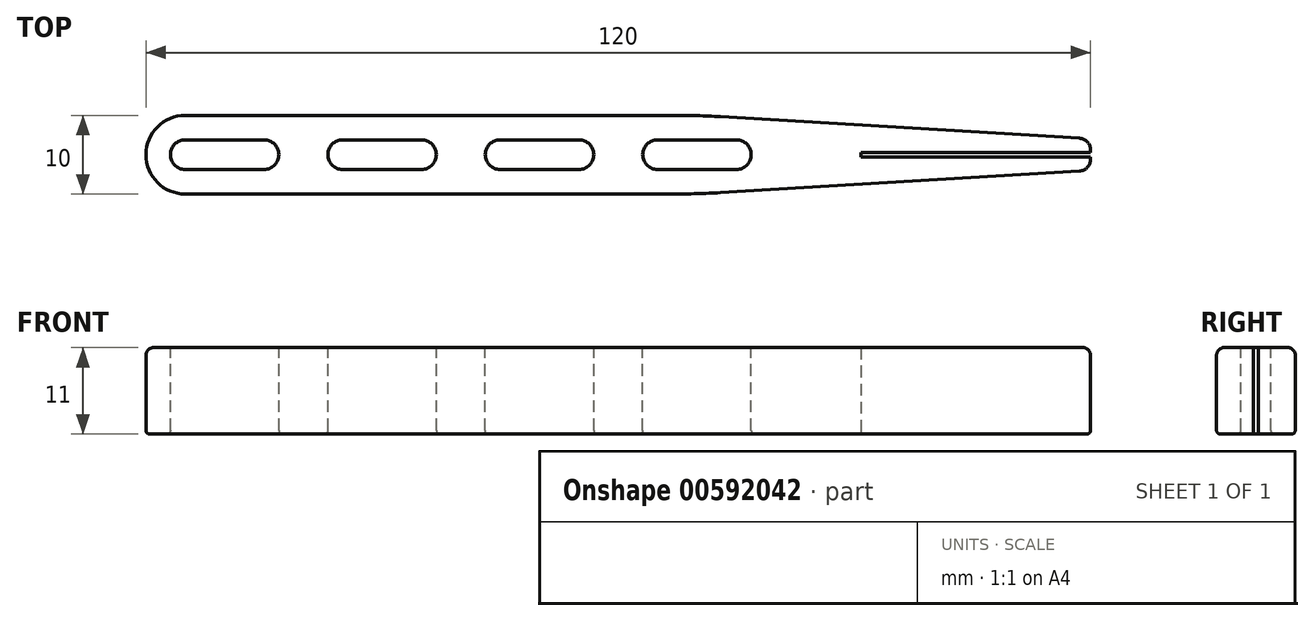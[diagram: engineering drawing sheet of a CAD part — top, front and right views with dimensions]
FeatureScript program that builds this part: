
annotation { "Feature Type Name" : "Feature", "Feature Type Description" : "" }
export const myFeature = defineFeature(function(context is Context, id is Id, definition is map)
    precondition{}
    {
        {
            var Q0;
            Q0=qCreatedBy(makeId("Top.planeOp"),FACE);
            var sketch = newSketch(context, id + "F0", { "sketchPlane" : qUnion([Q0])});
            skLineSegment(sketch, "E0.bottom", {"start": v(-60.45, 1.98) * mm, "end": v(59.55, 1.98) * mm});
            skLineSegment(sketch, "E0.top", {"start": v(-60.45, -8.02) * mm, "end": v(59.55, -8.02) * mm});
            skLineSegment(sketch, "E0.left", {"start": v(-60.45, 1.98) * mm, "end": v(-60.45, -8.02) * mm});
            skLineSegment(sketch, "E1", {"start": v(59.55, -2.72) * mm, "end": v(30.4, -2.72) * mm});
            skLineSegment(sketch, "E2", {"start": v(30.4, -2.72) * mm, "end": v(30.4, -3.32) * mm});
            skLineSegment(sketch, "E3", {"start": v(30.4, -3.32) * mm, "end": v(59.55, -3.32) * mm});
            skLineSegment(sketch, "E4", {"start": v(59.55, 1.98) * mm, "end": v(59.55, -2.72) * mm});
            skLineSegment(sketch, "E5", {"start": v(59.55, -8.02) * mm, "end": v(59.55, -3.32) * mm});
            skSolve(sketch);
        }
        {
            var Q0;
            Q0=makeQuery(id+"F0.imprint","IMPRINT",FACE,{"disambiguationData":[TD([[makeQuery(id+"F0.imprint","IMPRINT",EDGE,{"derivedFrom":sQuery(id+"F0.wireOp",EDGE,"E0.bottom")}),-1.0]])]});
            extrude(context, id + "F1", {"entities" : qUnion([Q0]), "depth" : 11 * mm, "offsetDistance" : 25 * mm});
        }
        {
            var Q0;
            Q0=makeQuery(id+"F1.opExtrude","SWEPT_EDGE",EDGE,{"disambiguationData":[OSD([sQuery(id+"F0.wireOp",EDGE,"E0.top"),sQuery(id+"F0.wireOp",EDGE,"E5")])]});
            chamfer(context, id + "F2", {"entities" : qUnion([Q0]), "chamferType" : ChamferType.TWO_OFFSETS, "width1" : 3 * mm, "oppositeDirection" : false, "width2" : 50 * mm, "tangentPropagation" : true});
        }
        {
            var Q0;
            Q0=makeQuery(id+"F1.opExtrude","SWEPT_EDGE",EDGE,{"disambiguationData":[OSD([sQuery(id+"F0.wireOp",EDGE,"E0.bottom"),sQuery(id+"F0.wireOp",EDGE,"E4")])]});
            chamfer(context, id + "F3", {"entities" : qUnion([Q0]), "chamferType" : ChamferType.TWO_OFFSETS, "width1" : 3 * mm, "oppositeDirection" : true, "width2" : 50 * mm, "tangentPropagation" : true});
        }
        {
            var Q0;
            {var subQ0=sQuery(id+"F0.wireOp",EDGE,"E4");Q0=makeQuery(id+"F3.opChamfer","BLEND_EDGE",EDGE,{"blendedFrom":[makeQuery(id+"F1.opExtrude","SWEPT_EDGE",EDGE,{"disambiguationData":[OSD([sQuery(id+"F0.wireOp",EDGE,"E0.bottom"),subQ0])]}),makeQuery(id+"F1.opExtrude","SWEPT_FACE",FACE,{"disambiguationData":[OSD([subQ0])]})],"blendedInto":[makeQuery(id+"F1.opExtrude","SWEPT_FACE",FACE,{"disambiguationData":[OSD([subQ0])]})]});}
            var Q1;
            {var subQ0=sQuery(id+"F0.wireOp",EDGE,"E5");Q1=makeQuery(id+"F2.opChamfer","BLEND_EDGE",EDGE,{"blendedFrom":[makeQuery(id+"F1.opExtrude","SWEPT_EDGE",EDGE,{"disambiguationData":[OSD([sQuery(id+"F0.wireOp",EDGE,"E0.top"),subQ0])]}),makeQuery(id+"F1.opExtrude","SWEPT_FACE",FACE,{"disambiguationData":[OSD([subQ0])]})],"blendedInto":[makeQuery(id+"F1.opExtrude","SWEPT_FACE",FACE,{"disambiguationData":[OSD([subQ0])]})]});}
            fillet(context, id + "F4", {"entities" : qUnion([Q0, Q1]), "radius" : 1.5 * mm, "tangentPropagation" : true, "allowEdgeOverflow" : false});
        }
        {
            var Q0;
            {var subQ0=sQuery(id+"F0.wireOp",EDGE,"E0.top");Q0=makeQuery(id+"F2.opChamfer","BLEND_EDGE",EDGE,{"blendedFrom":[makeQuery(id+"F1.opExtrude","SWEPT_EDGE",EDGE,{"disambiguationData":[OSD([subQ0,sQuery(id+"F0.wireOp",EDGE,"E5")])]}),makeQuery(id+"F1.opExtrude","SWEPT_FACE",FACE,{"disambiguationData":[OSD([subQ0])]})],"blendedInto":[makeQuery(id+"F1.opExtrude","SWEPT_FACE",FACE,{"disambiguationData":[OSD([subQ0])]})]});}
            var Q1;
            {var subQ0=sQuery(id+"F0.wireOp",EDGE,"E0.bottom");Q1=makeQuery(id+"F3.opChamfer","BLEND_EDGE",EDGE,{"blendedFrom":[makeQuery(id+"F1.opExtrude","SWEPT_EDGE",EDGE,{"disambiguationData":[OSD([subQ0,sQuery(id+"F0.wireOp",EDGE,"E4")])]}),makeQuery(id+"F1.opExtrude","SWEPT_FACE",FACE,{"disambiguationData":[OSD([subQ0])]})],"blendedInto":[makeQuery(id+"F1.opExtrude","SWEPT_FACE",FACE,{"disambiguationData":[OSD([subQ0])]})]});}
            fillet(context, id + "F5", {"entities" : qUnion([Q0, Q1]), "radius" : 100 * mm, "tangentPropagation" : true, "allowEdgeOverflow" : false});
        }
        {
            var Q0;
            Q0=makeQuery(id+"F1.opExtrude","CAP_FACE",FACE,{"disambiguationData":[OSD([sQuery(id+"F0.wireOp",EDGE,"E0.bottom"),sQuery(id+"F0.wireOp",EDGE,"E0.top"),sQuery(id+"F0.wireOp",EDGE,"E0.left"),sQuery(id+"F0.wireOp",EDGE,"E1"),sQuery(id+"F0.wireOp",EDGE,"E2"),sQuery(id+"F0.wireOp",EDGE,"E3"),sQuery(id+"F0.wireOp",EDGE,"E4"),sQuery(id+"F0.wireOp",EDGE,"E5")])],"isStart":false});
            var sketch = newSketch(context, id + "F6", { "sketchPlane" : qUnion([Q0])});
            skLineSegment(sketch, "E6", {"start": v(-59.45, -3.02) * mm, "end": v(30.4, -3.02) * mm, "construction": true});
            skCircle(sketch, "E7", {"center": v(-55.45, -3.02) * mm, "radius": 1.89 * mm});
            skCircle(sketch, "E8.1.0.0", {"center": v(-45.45, -3.02) * mm, "radius": 1.89 * mm});
            skCircle(sketch, "E8.2.0.0", {"center": v(-35.45, -3.02) * mm, "radius": 1.89 * mm});
            skCircle(sketch, "E8.3.0.0", {"center": v(-25.45, -3.02) * mm, "radius": 1.89 * mm});
            skCircle(sketch, "E8.4.0.0", {"center": v(-15.45, -3.02) * mm, "radius": 1.89 * mm});
            skCircle(sketch, "E8.5.0.0", {"center": v(-5.45, -3.02) * mm, "radius": 1.89 * mm});
            skCircle(sketch, "E8.6.0.0", {"center": v(4.55, -3.02) * mm, "radius": 1.89 * mm});
            skCircle(sketch, "E8.7.0.0", {"center": v(14.55, -3.02) * mm, "radius": 1.89 * mm});
            skLineSegment(sketch, "E8.direction1", {"start": v(-55.45, -3.02) * mm, "end": v(-45.45, -3.02) * mm, "construction": true});
            skLineSegment(sketch, "E9", {"start": v(-55.45, -1.13) * mm, "end": v(-45.45, -1.13) * mm});
            skLineSegment(sketch, "E10", {"start": v(-55.45, -4.9) * mm, "end": v(-45.45, -4.9) * mm});
            skLineSegment(sketch, "E11", {"start": v(-35.45, -1.13) * mm, "end": v(-25.45, -1.13) * mm});
            skLineSegment(sketch, "E12", {"start": v(-25.45, -4.9) * mm, "end": v(-35.45, -4.9) * mm});
            skLineSegment(sketch, "E13", {"start": v(-15.45, -4.9) * mm, "end": v(-5.45, -4.9) * mm});
            skLineSegment(sketch, "E14", {"start": v(-5.45, -1.13) * mm, "end": v(-15.45, -1.13) * mm});
            skLineSegment(sketch, "E15", {"start": v(4.55, -1.13) * mm, "end": v(14.55, -1.13) * mm});
            skLineSegment(sketch, "E16", {"start": v(14.55, -4.9) * mm, "end": v(4.55, -4.9) * mm});
            skSolve(sketch);
        }
        {
            var Q0;
            {var subQ0=sQuery(id+"F6.wireOp",EDGE,"E7");var subQ1=makeQuery(id+"F6.imprint","INTERSECT",VERTEX,{"derivedFrom":[subQ0,sQuery(id+"F6.wireOp",EDGE,"E9")]});Q0=makeQuery(id+"F6.imprint","IMPRINT",FACE,{"disambiguationData":[TD([[makeQuery(id+"F6.imprint","IMPRINT",EDGE,{"disambiguationData":[TD([[subQ1,-1.0]])],"derivedFrom":subQ0}),1.0]])]});}
            var Q1;
            {var subQ0=sQuery(id+"F6.wireOp",EDGE,"E9");Q1=makeQuery(id+"F6.imprint","IMPRINT",FACE,{"disambiguationData":[TD([[makeQuery(id+"F6.imprint","IMPRINT",EDGE,{"derivedFrom":subQ0}),-1.0]])]});}
            var Q2;
            {var subQ0=sQuery(id+"F6.wireOp",EDGE,"E8.1.0.0");var subQ1=makeQuery(id+"F6.imprint","INTERSECT",VERTEX,{"derivedFrom":[subQ0,sQuery(id+"F6.wireOp",EDGE,"E9")]});Q2=makeQuery(id+"F6.imprint","IMPRINT",FACE,{"disambiguationData":[TD([[makeQuery(id+"F6.imprint","IMPRINT",EDGE,{"disambiguationData":[TD([[subQ1,-1.0]])],"derivedFrom":subQ0}),1.0]])]});}
            var Q3;
            {var subQ0=sQuery(id+"F6.wireOp",EDGE,"E8.2.0.0");var subQ1=makeQuery(id+"F6.imprint","INTERSECT",VERTEX,{"derivedFrom":[subQ0,sQuery(id+"F6.wireOp",EDGE,"E11")]});Q3=makeQuery(id+"F6.imprint","IMPRINT",FACE,{"disambiguationData":[TD([[makeQuery(id+"F6.imprint","IMPRINT",EDGE,{"disambiguationData":[TD([[subQ1,-1.0]])],"derivedFrom":subQ0}),1.0]])]});}
            var Q4;
            {var subQ0=sQuery(id+"F6.wireOp",EDGE,"E11");Q4=makeQuery(id+"F6.imprint","IMPRINT",FACE,{"disambiguationData":[TD([[makeQuery(id+"F6.imprint","IMPRINT",EDGE,{"derivedFrom":subQ0}),-1.0]])]});}
            var Q5;
            {var subQ0=sQuery(id+"F6.wireOp",EDGE,"E8.3.0.0");var subQ1=makeQuery(id+"F6.imprint","INTERSECT",VERTEX,{"derivedFrom":[subQ0,sQuery(id+"F6.wireOp",EDGE,"E11")]});Q5=makeQuery(id+"F6.imprint","IMPRINT",FACE,{"disambiguationData":[TD([[makeQuery(id+"F6.imprint","IMPRINT",EDGE,{"disambiguationData":[TD([[subQ1,-1.0]])],"derivedFrom":subQ0}),1.0]])]});}
            var Q6;
            {var subQ0=sQuery(id+"F6.wireOp",EDGE,"E8.4.0.0");var subQ1=makeQuery(id+"F6.imprint","INTERSECT",VERTEX,{"derivedFrom":[subQ0,sQuery(id+"F6.wireOp",EDGE,"E13")]});Q6=makeQuery(id+"F6.imprint","IMPRINT",FACE,{"disambiguationData":[TD([[makeQuery(id+"F6.imprint","IMPRINT",EDGE,{"disambiguationData":[TD([[subQ1,1.0]])],"derivedFrom":subQ0}),1.0]])]});}
            var Q7;
            {var subQ0=sQuery(id+"F6.wireOp",EDGE,"E13");Q7=makeQuery(id+"F6.imprint","IMPRINT",FACE,{"disambiguationData":[TD([[makeQuery(id+"F6.imprint","IMPRINT",EDGE,{"derivedFrom":subQ0}),1.0]])]});}
            var Q8;
            {var subQ0=sQuery(id+"F6.wireOp",EDGE,"E8.5.0.0");var subQ1=makeQuery(id+"F6.imprint","INTERSECT",VERTEX,{"derivedFrom":[subQ0,sQuery(id+"F6.wireOp",EDGE,"E13")]});Q8=makeQuery(id+"F6.imprint","IMPRINT",FACE,{"disambiguationData":[TD([[makeQuery(id+"F6.imprint","IMPRINT",EDGE,{"disambiguationData":[TD([[subQ1,1.0]])],"derivedFrom":subQ0}),1.0]])]});}
            var Q9;
            {var subQ0=sQuery(id+"F6.wireOp",EDGE,"E8.6.0.0");var subQ1=makeQuery(id+"F6.imprint","INTERSECT",VERTEX,{"derivedFrom":[subQ0,sQuery(id+"F6.wireOp",EDGE,"E15")]});Q9=makeQuery(id+"F6.imprint","IMPRINT",FACE,{"disambiguationData":[TD([[makeQuery(id+"F6.imprint","IMPRINT",EDGE,{"disambiguationData":[TD([[subQ1,-1.0]])],"derivedFrom":subQ0}),1.0]])]});}
            var Q10;
            {var subQ0=sQuery(id+"F6.wireOp",EDGE,"E15");Q10=makeQuery(id+"F6.imprint","IMPRINT",FACE,{"disambiguationData":[TD([[makeQuery(id+"F6.imprint","IMPRINT",EDGE,{"derivedFrom":subQ0}),-1.0]])]});}
            var Q11;
            {var subQ0=sQuery(id+"F6.wireOp",EDGE,"E8.7.0.0");var subQ1=makeQuery(id+"F6.imprint","INTERSECT",VERTEX,{"derivedFrom":[subQ0,sQuery(id+"F6.wireOp",EDGE,"E15")]});Q11=makeQuery(id+"F6.imprint","IMPRINT",FACE,{"disambiguationData":[TD([[makeQuery(id+"F6.imprint","IMPRINT",EDGE,{"disambiguationData":[TD([[subQ1,-1.0]])],"derivedFrom":subQ0}),1.0]])]});}
            extrude(context, id + "F7", {"entities" : qUnion([Q0, Q1, Q2, Q3, Q4, Q5, Q6, Q7, Q8, Q9, Q10, Q11]), "operationType" : NewBodyOperationType.REMOVE, "oppositeDirection" : true, "depth" : 25 * mm, "offsetDistance" : 25 * mm});
        }
        {
            var Q0;
            {var subQ0=sQuery(id+"F0.wireOp",EDGE,"E5");var subQ1=sQuery(id+"F0.wireOp",EDGE,"E0.top");Q0=makeQuery(id+"F2.opChamfer","BLEND_EDGE",EDGE,{"blendedFrom":[makeQuery(id+"F1.opExtrude","SWEPT_EDGE",EDGE,{"disambiguationData":[OSD([subQ1,subQ0])]}),makeQuery(id+"F1.opExtrude","CAP_FACE",FACE,{"disambiguationData":[OSD([sQuery(id+"F0.wireOp",EDGE,"E0.bottom"),subQ1,sQuery(id+"F0.wireOp",EDGE,"E0.left"),sQuery(id+"F0.wireOp",EDGE,"E1"),sQuery(id+"F0.wireOp",EDGE,"E2"),sQuery(id+"F0.wireOp",EDGE,"E3"),sQuery(id+"F0.wireOp",EDGE,"E4"),subQ0])],"isStart":true})],"blendedInto":[makeQuery(id+"F1.opExtrude","CAP_FACE",FACE,{"disambiguationData":[OSD([sQuery(id+"F0.wireOp",EDGE,"E0.bottom"),subQ1,sQuery(id+"F0.wireOp",EDGE,"E0.left"),sQuery(id+"F0.wireOp",EDGE,"E1"),sQuery(id+"F0.wireOp",EDGE,"E2"),sQuery(id+"F0.wireOp",EDGE,"E3"),sQuery(id+"F0.wireOp",EDGE,"E4"),subQ0])],"isStart":true})]});}
            var Q1;
            {var subQ0=sQuery(id+"F0.wireOp",EDGE,"E4");var subQ1=sQuery(id+"F0.wireOp",EDGE,"E0.bottom");Q1=makeQuery(id+"F5.opFillet","BLEND_EDGE",EDGE,{"blendedFrom":[makeQuery(id+"F3.opChamfer","BLEND_EDGE",EDGE,{"blendedFrom":[makeQuery(id+"F1.opExtrude","SWEPT_EDGE",EDGE,{"disambiguationData":[OSD([subQ1,subQ0])]}),makeQuery(id+"F1.opExtrude","SWEPT_FACE",FACE,{"disambiguationData":[OSD([subQ1])]})],"blendedInto":[makeQuery(id+"F1.opExtrude","SWEPT_FACE",FACE,{"disambiguationData":[OSD([subQ1])]})]}),makeQuery(id+"F1.opExtrude","CAP_FACE",FACE,{"disambiguationData":[OSD([subQ1,sQuery(id+"F0.wireOp",EDGE,"E0.top"),sQuery(id+"F0.wireOp",EDGE,"E0.left"),sQuery(id+"F0.wireOp",EDGE,"E1"),sQuery(id+"F0.wireOp",EDGE,"E2"),sQuery(id+"F0.wireOp",EDGE,"E3"),subQ0,sQuery(id+"F0.wireOp",EDGE,"E5")])],"isStart":true})],"blendedInto":[makeQuery(id+"F1.opExtrude","CAP_FACE",FACE,{"disambiguationData":[OSD([subQ1,sQuery(id+"F0.wireOp",EDGE,"E0.top"),sQuery(id+"F0.wireOp",EDGE,"E0.left"),sQuery(id+"F0.wireOp",EDGE,"E1"),sQuery(id+"F0.wireOp",EDGE,"E2"),sQuery(id+"F0.wireOp",EDGE,"E3"),subQ0,sQuery(id+"F0.wireOp",EDGE,"E5")])],"isStart":true})]});}
            var Q2;
            Q2=makeQuery(id+"F1.opExtrude","CAP_EDGE",EDGE,{"disambiguationData":[OSD([sQuery(id+"F0.wireOp",EDGE,"E0.left")])],"isStart":true});
            var Q3;
            Q3=makeQuery(id+"F7.boolean.opBoolean","INTERSECT",EDGE,{"derivedFrom":[makeQuery(id+"F1.opExtrude","CAP_FACE",FACE,{"disambiguationData":[OSD([sQuery(id+"F0.wireOp",EDGE,"E0.bottom"),sQuery(id+"F0.wireOp",EDGE,"E0.top"),sQuery(id+"F0.wireOp",EDGE,"E0.left"),sQuery(id+"F0.wireOp",EDGE,"E1"),sQuery(id+"F0.wireOp",EDGE,"E2"),sQuery(id+"F0.wireOp",EDGE,"E3"),sQuery(id+"F0.wireOp",EDGE,"E4"),sQuery(id+"F0.wireOp",EDGE,"E5")])],"isStart":true}),makeQuery(id+"F7.opExtrude","SWEPT_FACE",FACE,{"disambiguationData":[OSD([sQuery(id+"F6.wireOp",EDGE,"E8.1.0.0")])]})]});
            var Q4;
            Q4=makeQuery(id+"F7.boolean.opBoolean","INTERSECT",EDGE,{"derivedFrom":[makeQuery(id+"F1.opExtrude","CAP_FACE",FACE,{"disambiguationData":[OSD([sQuery(id+"F0.wireOp",EDGE,"E0.bottom"),sQuery(id+"F0.wireOp",EDGE,"E0.top"),sQuery(id+"F0.wireOp",EDGE,"E0.left"),sQuery(id+"F0.wireOp",EDGE,"E1"),sQuery(id+"F0.wireOp",EDGE,"E2"),sQuery(id+"F0.wireOp",EDGE,"E3"),sQuery(id+"F0.wireOp",EDGE,"E4"),sQuery(id+"F0.wireOp",EDGE,"E5")])],"isStart":true}),makeQuery(id+"F7.opExtrude","SWEPT_FACE",FACE,{"disambiguationData":[OSD([sQuery(id+"F6.wireOp",EDGE,"E8.3.0.0")])]})]});
            var Q5;
            Q5=makeQuery(id+"F7.boolean.opBoolean","INTERSECT",EDGE,{"derivedFrom":[makeQuery(id+"F1.opExtrude","CAP_FACE",FACE,{"disambiguationData":[OSD([sQuery(id+"F0.wireOp",EDGE,"E0.bottom"),sQuery(id+"F0.wireOp",EDGE,"E0.top"),sQuery(id+"F0.wireOp",EDGE,"E0.left"),sQuery(id+"F0.wireOp",EDGE,"E1"),sQuery(id+"F0.wireOp",EDGE,"E2"),sQuery(id+"F0.wireOp",EDGE,"E3"),sQuery(id+"F0.wireOp",EDGE,"E4"),sQuery(id+"F0.wireOp",EDGE,"E5")])],"isStart":true}),makeQuery(id+"F7.opExtrude","SWEPT_FACE",FACE,{"disambiguationData":[OSD([sQuery(id+"F6.wireOp",EDGE,"E8.5.0.0")])]})]});
            var Q6;
            Q6=makeQuery(id+"F7.boolean.opBoolean","INTERSECT",EDGE,{"derivedFrom":[makeQuery(id+"F1.opExtrude","CAP_FACE",FACE,{"disambiguationData":[OSD([sQuery(id+"F0.wireOp",EDGE,"E0.bottom"),sQuery(id+"F0.wireOp",EDGE,"E0.top"),sQuery(id+"F0.wireOp",EDGE,"E0.left"),sQuery(id+"F0.wireOp",EDGE,"E1"),sQuery(id+"F0.wireOp",EDGE,"E2"),sQuery(id+"F0.wireOp",EDGE,"E3"),sQuery(id+"F0.wireOp",EDGE,"E4"),sQuery(id+"F0.wireOp",EDGE,"E5")])],"isStart":true}),makeQuery(id+"F7.opExtrude","SWEPT_FACE",FACE,{"disambiguationData":[OSD([sQuery(id+"F6.wireOp",EDGE,"E8.7.0.0")])]})]});
            fillet(context, id + "F8", {"entities" : qUnion([Q0, Q1, Q2, Q3, Q4, Q5, Q6]), "radius" : 0.5 * mm, "tangentPropagation" : true, "allowEdgeOverflow" : false});
        }
        {
            var Q0;
            Q0=makeQuery(id+"F1.opExtrude","CAP_EDGE",EDGE,{"disambiguationData":[OSD([sQuery(id+"F0.wireOp",EDGE,"E0.bottom")])],"isStart":false});
            var Q1;
            Q1=makeQuery(id+"F1.opExtrude","CAP_EDGE",EDGE,{"disambiguationData":[OSD([sQuery(id+"F0.wireOp",EDGE,"E0.top")])],"isStart":false});
            var Q2;
            Q2=makeQuery(id+"F1.opExtrude","CAP_EDGE",EDGE,{"disambiguationData":[OSD([sQuery(id+"F0.wireOp",EDGE,"E0.left")])],"isStart":false});
            var Q3;
            Q3=makeQuery(id+"F7.boolean.opBoolean","COPY",EDGE,{"derivedFrom":makeQuery(id+"F7.opExtrude","CAP_EDGE",EDGE,{"disambiguationData":[OSD([sQuery(id+"F6.wireOp",EDGE,"E8.1.0.0")])],"isStart":true})});
            var Q4;
            Q4=makeQuery(id+"F7.boolean.opBoolean","COPY",EDGE,{"derivedFrom":makeQuery(id+"F7.opExtrude","CAP_EDGE",EDGE,{"disambiguationData":[OSD([sQuery(id+"F6.wireOp",EDGE,"E8.3.0.0")])],"isStart":true})});
            var Q5;
            Q5=makeQuery(id+"F7.boolean.opBoolean","COPY",EDGE,{"derivedFrom":makeQuery(id+"F7.opExtrude","CAP_EDGE",EDGE,{"disambiguationData":[OSD([sQuery(id+"F6.wireOp",EDGE,"E8.5.0.0")])],"isStart":true})});
            var Q6;
            Q6=makeQuery(id+"F7.boolean.opBoolean","COPY",EDGE,{"derivedFrom":makeQuery(id+"F7.opExtrude","CAP_EDGE",EDGE,{"disambiguationData":[OSD([sQuery(id+"F6.wireOp",EDGE,"E8.7.0.0")])],"isStart":true})});
            fillet(context, id + "F9", {"entities" : qUnion([Q0, Q1, Q2, Q3, Q4, Q5, Q6]), "radius" : 1 * mm, "tangentPropagation" : true, "allowEdgeOverflow" : false});
        }
        {
            var Q0;
            Q0=makeQuery(id+"F1.opExtrude","SWEPT_EDGE",EDGE,{"disambiguationData":[OSD([sQuery(id+"F0.wireOp",EDGE,"E0.bottom"),sQuery(id+"F0.wireOp",EDGE,"E0.left")])]});
            var Q1;
            Q1=makeQuery(id+"F1.opExtrude","SWEPT_EDGE",EDGE,{"disambiguationData":[OSD([sQuery(id+"F0.wireOp",EDGE,"E0.top"),sQuery(id+"F0.wireOp",EDGE,"E0.left")])]});
            fillet(context, id + "F10", {"entities" : qUnion([Q0, Q1]), "radius" : 5 * mm, "tangentPropagation" : true, "allowEdgeOverflow" : false});
        }
    });
